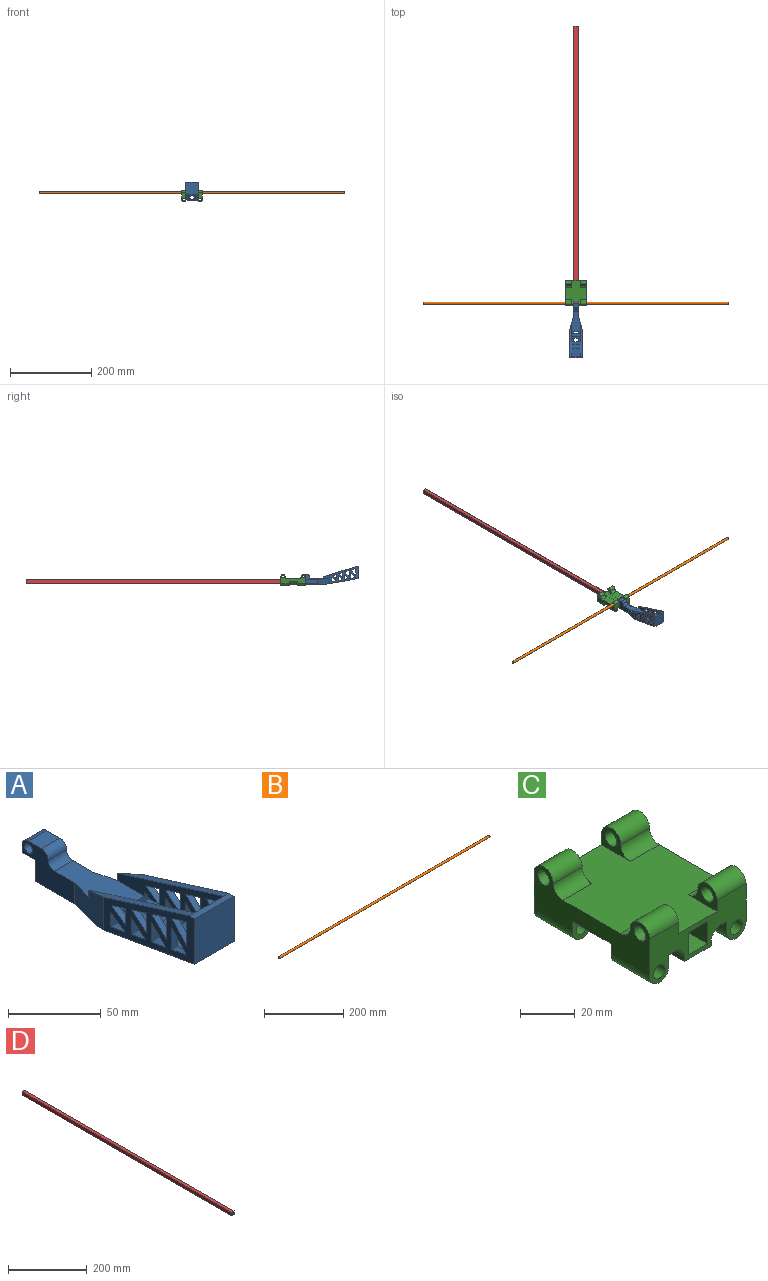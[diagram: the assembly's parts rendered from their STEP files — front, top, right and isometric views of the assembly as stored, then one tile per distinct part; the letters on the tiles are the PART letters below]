
ASSEMBLY  parts=4 mates=3
PART A: 74 faces, bbox 30x140x44 mm
  f0: plane 10x9.31mm, normal (0,0,-1), area 93.1mm2, adj f2,f7,f38,f46
  f1: plane 65.86x10mm, normal (0,0,-1), area 658.6mm2, adj f2,f7,f21,f47
  f2: plane 118.57x10mm, normal (-1,0,0), area 845.8mm2, adj f0,f1,f14,f15,f16,f21,f37,f38
  f3: plane 22x7.49mm, normal (0,0,1), area 164.9mm2, adj f10,f11,f39,f58
  f4: plane 22x6.85mm, normal (0,0,1), area 150.6mm2, adj f10,f11,f42,f46
  f5: plane 22x4mm, normal (0,0,1), area 88mm2, adj f10,f11,f38,f44
  f6: plane 50.86x22mm, normal (0,0,1), area 938.6mm2, adj f10,f11,f17,f19,f28,f32,f33,f47
  f7: plane 118.57x10mm, normal (1,0,0), area 845.8mm2, adj f0,f1,f14,f15,f16,f21,f38,f39
  f8: plane 70x42.25mm, normal (-1,0,0), area 1261.2mm2, adj f13,f14,f29,f30,f32,f34,f35,f36
  f9: plane 70.14x42.28mm, normal (1,0,0), area 1264.3mm2, adj f12,f14,f29,f30,f33,f37,f38,f39
  f10: plane 81.07x30mm, normal (-1,0,0), area 909.6mm2, adj f3,f4,f5,f6,f12,f18,f31,f33
  f11: plane 80.93x30mm, normal (1,0,0), area 908.9mm2, adj f3,f4,f5,f6,f13,f18,f31,f32
  f12: plane 81.07x25.34mm, normal (0,0.3,0.95), area 308.5mm2, adj f9,f10,f30,f33
  f13: plane 80.93x25.29mm, normal (0,0.3,0.95), area 307.9mm2, adj f8,f11,f30,f32
  f14: plane 80x30mm, normal (0,-0.17,-0.99), area 1829.5mm2, adj f2,f7,f8,f9,f15,f16,f20,f29
  f15: plane 26.81x10mm, normal (0,0,-1), area 268.1mm2, adj f2,f7,f14,f39
  f16: plane 61.43x10mm, normal (0,0,1), area 614.3mm2, adj f2,f7,f14,f21
  f17: plane 40x24mm, normal (1,0,0), area 586.4mm2, adj f6,f20,f21,f22,f23,f24,f25,f26
  f18: plane 22x19.2mm, normal (0,0,1), area 422.5mm2, adj f10,f11,f31,f57
  f19: plane 40.14x24mm, normal (-1,0,0), area 588.4mm2, adj f6,f20,f21,f22,f23,f24,f25,f26
  f20: plane 50x24.68mm, normal (0,0,-1), area 806.4mm2, adj f14,f17,f19,f21,f32,f33
  f21: plane 14x14mm, normal (0,1,0), area 96mm2, adj f1,f2,f7,f16,f17,f19,f20,f22
  f22: plane 14x10mm, normal (0,0,-1), area 140mm2, adj f17,f19,f21,f25
  f23: plane 14x10mm, normal (0,0,1), area 140mm2, adj f17,f19,f26,f27
  f24: cylinder r=3mm len=14mm, axis (-1,0,0), area 263.9mm2, adj f17,f19
  f25: plane 14x5mm, normal (0,1,0), area 70mm2, adj f17,f19,f22,f26
  f26: cylinder r=5mm len=14mm, axis (-1,0,0), area 110mm2, adj f17,f19,f23,f25
  f27: cylinder r=5mm len=14mm, axis (1,0,0), area 110mm2, adj f17,f19,f23,f28
  f28: cylinder r=5mm len=14mm, axis (1,0,0), area 110mm2, adj f6,f17,f19,f27
  f29: plane 30x30mm, normal (0,-1,0), area 900mm2, adj f8,f9,f14,f30
  f30: plane 30x4mm, normal (0,0,1), area 120mm2, adj f8,f9,f12,f13,f29,f31
  f31: plane 30x22mm, normal (0,1,0), area 660mm2, adj f10,f11,f18,f30
  f32: plane 29.86x23.38mm, normal (-0.97,0.26,0), area 532.5mm2, adj f6,f8,f11,f13,f14,f19,f20
  f33: plane 29.86x23.33mm, normal (0.97,0.26,0), area 532.1mm2, adj f6,f9,f10,f12,f14,f17,f20
  f34: plane 16.54x4mm, normal (0,1,0), area 66.1mm2, adj f8,f11,f35,f36
  f35: plane 11.44x4mm, normal (0,-0.3,-0.95), area 48mm2, adj f8,f11,f34,f36
  f36: plane 12.96x11.44mm, normal (0,-0.75,0.66), area 69.2mm2, adj f8,f11,f34,f35
  f37: plane 10.98x10mm, normal (0,0.17,0.99), area 111.5mm2, adj f2,f9,f38,f39
  f38: plane 30x11.34mm, normal (0,-1,0), area 164.1mm2, adj f0,f2,f5,f7,f8,f9,f10,f11
  f39: plane 30x10.98mm, normal (0,0.65,-0.76), area 193mm2, adj f2,f3,f7,f8,f9,f10,f11,f15
  f40: plane 10.98x10mm, normal (0,0.17,0.99), area 111.5mm2, adj f7,f8,f38,f39
  f41: plane 11.15x4mm, normal (0,-0.3,-0.95), area 46.7mm2, adj f9,f10,f42,f44
  f42: plane 30x11.15mm, normal (0,-0.58,0.81), area 143.5mm2, adj f4,f8,f9,f10,f11,f41,f43,f44
  f43: plane 11.15x4mm, normal (0,-0.3,-0.95), area 46.7mm2, adj f8,f11,f42,f44
  f44: plane 30x11.51mm, normal (0,1,0), area 111.7mm2, adj f5,f8,f9,f10,f11,f41,f42,f43
  f45: plane 10.78x10mm, normal (0,0.17,0.99), area 109.5mm2, adj f2,f9,f46,f47
  f46: plane 30x10.78mm, normal (0,0.58,-0.81), area 248.9mm2, adj f0,f2,f4,f7,f8,f9,f10,f11
  f47: plane 30x9.65mm, normal (0,-1,0), area 183.2mm2, adj f1,f2,f6,f7,f8,f9,f10,f11
  f48: plane 10.78x10mm, normal (0,0.17,0.99), area 109.5mm2, adj f7,f8,f46,f47
  f49: plane 14.68x4mm, normal (0,-1,0), area 58.7mm2, adj f8,f11,f50,f51
  f50: plane 11.23x4mm, normal (0,0.17,0.99), area 45.6mm2, adj f8,f11,f49,f51
  f51: plane 12.71x11.23mm, normal (0,0.75,-0.66), area 67.8mm2, adj f8,f11,f49,f50
  f52: plane 14.88x4mm, normal (0,1,0), area 59.5mm2, adj f8,f11,f53,f54
  f53: plane 11.38x4mm, normal (0,-0.3,-0.95), area 47.7mm2, adj f8,f11,f52,f54
  f54: plane 11.38x11.32mm, normal (0,-0.71,0.71), area 64.2mm2, adj f8,f11,f52,f53
  f55: plane 11.12x11.07mm, normal (0,0.71,-0.71), area 62.8mm2, adj f9,f10,f57,f58
  f56: plane 11.12x11.07mm, normal (0,0.71,-0.71), area 62.8mm2, adj f8,f11,f57,f58
  f57: plane 30x11.12mm, normal (0,0.17,0.99), area 310.7mm2, adj f8,f9,f10,f11,f18,f55,f56,f58
  f58: plane 30x13.02mm, normal (0,-1,0), area 142.1mm2, adj f3,f8,f9,f10,f11,f55,f56,f57
  f59: plane 13.2x4mm, normal (0,1,0), area 52.8mm2, adj f8,f11,f60,f61
  f60: plane 11.28x4mm, normal (0,-0.3,-0.95), area 47.3mm2, adj f8,f11,f59,f61
  f61: plane 11.28x9.68mm, normal (0,-0.65,0.76), area 59.5mm2, adj f8,f11,f59,f60
  f62: plane 12.96x11.44mm, normal (0,-0.75,0.66), area 69.2mm2, adj f9,f10,f63,f64
  f63: plane 11.44x4mm, normal (0,-0.3,-0.95), area 48mm2, adj f9,f10,f62,f64
  f64: plane 16.54x4mm, normal (0,1,0), area 66.1mm2, adj f9,f10,f62,f63
  f65: plane 12.71x11.23mm, normal (0,0.75,-0.66), area 67.8mm2, adj f9,f10,f66,f67
  f66: plane 11.23x4mm, normal (0,0.17,0.99), area 45.6mm2, adj f9,f10,f65,f67
  f67: plane 14.68x4mm, normal (0,-1,0), area 58.7mm2, adj f9,f10,f65,f66
  f68: plane 11.38x11.32mm, normal (0,-0.71,0.71), area 64.2mm2, adj f9,f10,f69,f70
  f69: plane 11.38x4mm, normal (0,-0.3,-0.95), area 47.7mm2, adj f9,f10,f68,f70
  f70: plane 14.88x4mm, normal (0,1,0), area 59.5mm2, adj f9,f10,f68,f69
  f71: plane 11.28x9.68mm, normal (0,-0.65,0.76), area 59.5mm2, adj f9,f10,f72,f73
  f72: plane 11.28x4mm, normal (0,-0.3,-0.95), area 47.3mm2, adj f9,f10,f71,f73
  f73: plane 13.2x4mm, normal (0,1,0), area 52.8mm2, adj f9,f10,f71,f72
PART B: 4 faces, bbox 750x6x6 mm
  f0: cylinder r=2.5mm len=750mm, axis (-1,0,0), area 11781mm2, adj f2,f3
  f1: cylinder r=3mm len=750mm, axis (-1,0,0), area 14137.2mm2, adj f2,f3
  f2: plane 6x6mm, normal (1,0,0), area 8.6mm2, adj f0,f1
  f3: plane 6x6mm, normal (-1,0,0), area 8.6mm2, adj f0,f1
PART C: 48 faces, bbox 50x60x27 mm
  f0: cylinder r=3mm len=15mm, axis (-1,0,0), area 282.7mm2, adj f3,f32
  f1: cylinder r=3mm len=15mm, axis (-1,0,0), area 282.7mm2, adj f3,f30
  f2: plane 20x5mm, normal (1,0,0), area 100mm2, adj f11,f18,f29,f38
  f3: plane 60x22mm, normal (-1,0,0), area 752.7mm2, adj f0,f1,f7,f11,f18,f19,f28,f29
  f4: cylinder r=3mm len=20mm, axis (0,-1,0), area 377mm2, adj f19,f28
  f5: plane 20x5mm, normal (-1,0,0), area 100mm2, adj f15,f18,f26,f39
  f6: cylinder r=3mm len=20mm, axis (0,-1,0), area 377mm2, adj f18,f26
  f7: plane 60x50mm, normal (0,0,1), area 2100mm2, adj f3,f16,f18,f19,f30,f31,f32,f33
  f8: plane 60x10mm, normal (0,0,-1), area 600mm2, adj f9,f17,f18,f19
  f9: plane 60x10mm, normal (-1,0,0), area 600mm2, adj f8,f10,f18,f19
  f10: plane 60x10mm, normal (0,0,1), area 600mm2, adj f9,f17,f18,f19
  f11: plane 60x13mm, normal (0,0,-1), area 380mm2, adj f2,f3,f18,f19,f23,f28,f29,f46
  f12: plane 60x2mm, normal (-1,0,0), area 120mm2, adj f13,f18,f19,f46
  f13: plane 60x14mm, normal (0,0,-1), area 840mm2, adj f12,f14,f18,f19
  f14: plane 60x2mm, normal (1,0,0), area 120mm2, adj f13,f18,f19,f47
  f15: plane 60x13mm, normal (0,0,-1), area 380mm2, adj f5,f16,f18,f19,f24,f26,f27,f47
  f16: plane 60x22mm, normal (1,0,0), area 752.7mm2, adj f7,f15,f18,f19,f20,f21,f26,f27
  f17: plane 60x10mm, normal (1,0,0), area 600mm2, adj f8,f10,f18,f19
  f18: plane 50x22mm, normal (0,-1,0), area 630.7mm2, adj f2,f3,f5,f6,f7,f8,f9,f10
  f19: plane 50x22mm, normal (0,1,0), area 630.7mm2, adj f3,f4,f7,f8,f9,f10,f11,f12
  f20: cylinder r=3mm len=15mm, axis (-1,0,0), area 282.7mm2, adj f16,f33
  f21: cylinder r=3mm len=15mm, axis (-1,0,0), area 282.7mm2, adj f16,f31
  f22: cylinder r=3mm len=20mm, axis (0,-1,0), area 377mm2, adj f18,f29
  f23: plane 20x5mm, normal (1,0,0), area 100mm2, adj f11,f19,f28,f41
  f24: plane 20x5mm, normal (-1,0,0), area 100mm2, adj f15,f19,f27,f40
  f25: cylinder r=3mm len=20mm, axis (0,-1,0), area 377mm2, adj f19,f27
  f26: plane 10x10mm, normal (0,1,0), area 61mm2, adj f5,f6,f15,f16,f39
  f27: plane 10x10mm, normal (0,-1,0), area 61mm2, adj f15,f16,f24,f25,f40
  f28: plane 10x10mm, normal (0,-1,0), area 61mm2, adj f3,f4,f11,f23,f41
  f29: plane 10x10mm, normal (0,1,0), area 61mm2, adj f2,f3,f11,f22,f38
  f30: plane 15x10mm, normal (1,0,0), area 66.4mm2, adj f1,f7,f19,f36,f37
  f31: plane 15x10mm, normal (-1,0,0), area 66.4mm2, adj f7,f19,f21,f44,f45
  f32: plane 15x10mm, normal (1,0,0), area 66.4mm2, adj f0,f7,f18,f34,f35
  f33: plane 15x10mm, normal (-1,0,0), area 66.4mm2, adj f7,f18,f20,f42,f43
  f34: cylinder r=5mm len=15mm, axis (1,0,0), area 117.8mm2, adj f3,f7,f32,f35
  f35: cylinder r=5mm len=15mm, axis (-1,0,0), area 235.6mm2, adj f3,f18,f32,f34
  f36: cylinder r=5mm len=15mm, axis (-1,0,0), area 117.8mm2, adj f3,f7,f30,f37
  f37: cylinder r=5mm len=15mm, axis (-1,0,0), area 235.6mm2, adj f3,f19,f30,f36
  f38: cylinder r=5mm len=20mm, axis (0,-1,0), area 314.2mm2, adj f2,f3,f18,f29
  f39: cylinder r=5mm len=20mm, axis (0,-1,0), area 314.2mm2, adj f5,f16,f18,f26
  f40: cylinder r=5mm len=20mm, axis (0,-1,0), area 314.2mm2, adj f16,f19,f24,f27
  f41: cylinder r=5mm len=20mm, axis (0,-1,0), area 314.2mm2, adj f3,f19,f23,f28
  f42: cylinder r=5mm len=15mm, axis (1,0,0), area 117.8mm2, adj f7,f16,f33,f43
  f43: cylinder r=5mm len=15mm, axis (-1,0,0), area 235.6mm2, adj f16,f18,f33,f42
  f44: cylinder r=5mm len=15mm, axis (-1,0,0), area 117.8mm2, adj f7,f16,f31,f45
  f45: cylinder r=5mm len=15mm, axis (-1,0,0), area 235.6mm2, adj f16,f19,f31,f44
  f46: cylinder r=5mm len=60mm, axis (0,1,0), area 471.2mm2, adj f11,f12,f18,f19
  f47: cylinder r=5mm len=60mm, axis (0,1,0), area 471.2mm2, adj f14,f15,f18,f19
PART D: 10 faces, bbox 10x750x10 mm
  f0: plane 750x8mm, normal (0,0,-1), area 6000mm2, adj f1,f7,f8,f9
  f1: plane 750x8mm, normal (-1,0,0), area 6000mm2, adj f0,f2,f8,f9
  f2: plane 750x8mm, normal (0,0,1), area 6000mm2, adj f1,f7,f8,f9
  f3: plane 750x10mm, normal (1,0,0), area 7500mm2, adj f4,f6,f8,f9
  f4: plane 750x10mm, normal (0,0,1), area 7500mm2, adj f3,f5,f8,f9
  f5: plane 750x10mm, normal (-1,0,0), area 7500mm2, adj f4,f6,f8,f9
  f6: plane 750x10mm, normal (0,0,-1), area 7500mm2, adj f3,f5,f8,f9
  f7: plane 750x8mm, normal (1,0,0), area 6000mm2, adj f0,f2,f8,f9
  f8: plane 10x10mm, normal (0,-1,0), area 36mm2, adj f0,f1,f2,f3,f4,f5,f6,f7
  f9: plane 10x10mm, normal (0,1,0), area 36mm2, adj f0,f1,f2,f3,f4,f5,f6,f7
PLACE A t=(-0.88,-26.92,1.88)mm
PLACE B t=(-0.88,-21.92,13.88)mm
PLACE C t=(-0.88,3.08,1.88)mm
PLACE D t=(-0.88,286.65,1.88)mm
MATE fastened D.f6 <-> A.f16  axis (0,0,-1) through (-0.88,-88.35,-3.12)mm
MATE fastened A.f21 <-> C.f18  axis (0,1,0) through (-0.88,-26.92,6.88)mm
MATE fastened B.f1 <-> A.f24  axis (-1,0,0) through (-0.88,-21.92,13.88)mm
